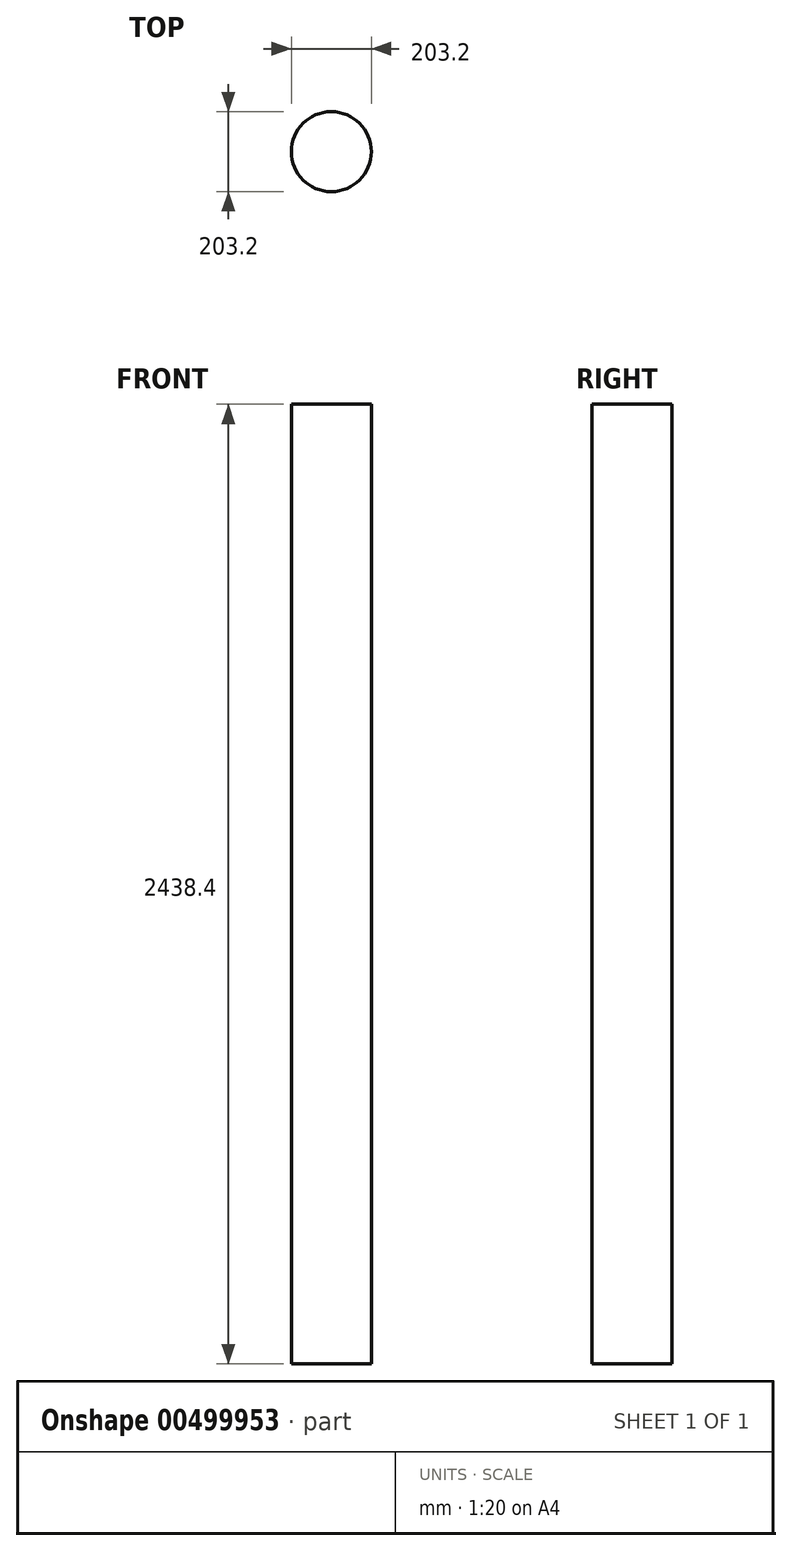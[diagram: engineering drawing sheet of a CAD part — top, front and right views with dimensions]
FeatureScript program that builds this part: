
annotation { "Feature Type Name" : "Feature", "Feature Type Description" : "" }
export const myFeature = defineFeature(function(context is Context, id is Id, definition is map)
    precondition{}
    {
        {
            var Q0;
            Q0=qCreatedBy(makeId("Top.planeOp"),FACE);
            var sketch = newSketch(context, id + "F0", { "sketchPlane" : qUnion([Q0])});
            skCircle(sketch, "E0", {"center": v(0, 0) * mm, "radius": 101.6 * mm});
            skSolve(sketch);
        }
        {
            var Q0;
            Q0 = qSketchRegion(id + "F0", true);
            extrude(context, id + "F1", {"entities" : qUnion([Q0]), "depth" : 2438.4 * mm, "offsetDistance" : 25.4 * mm});
        }
    });
